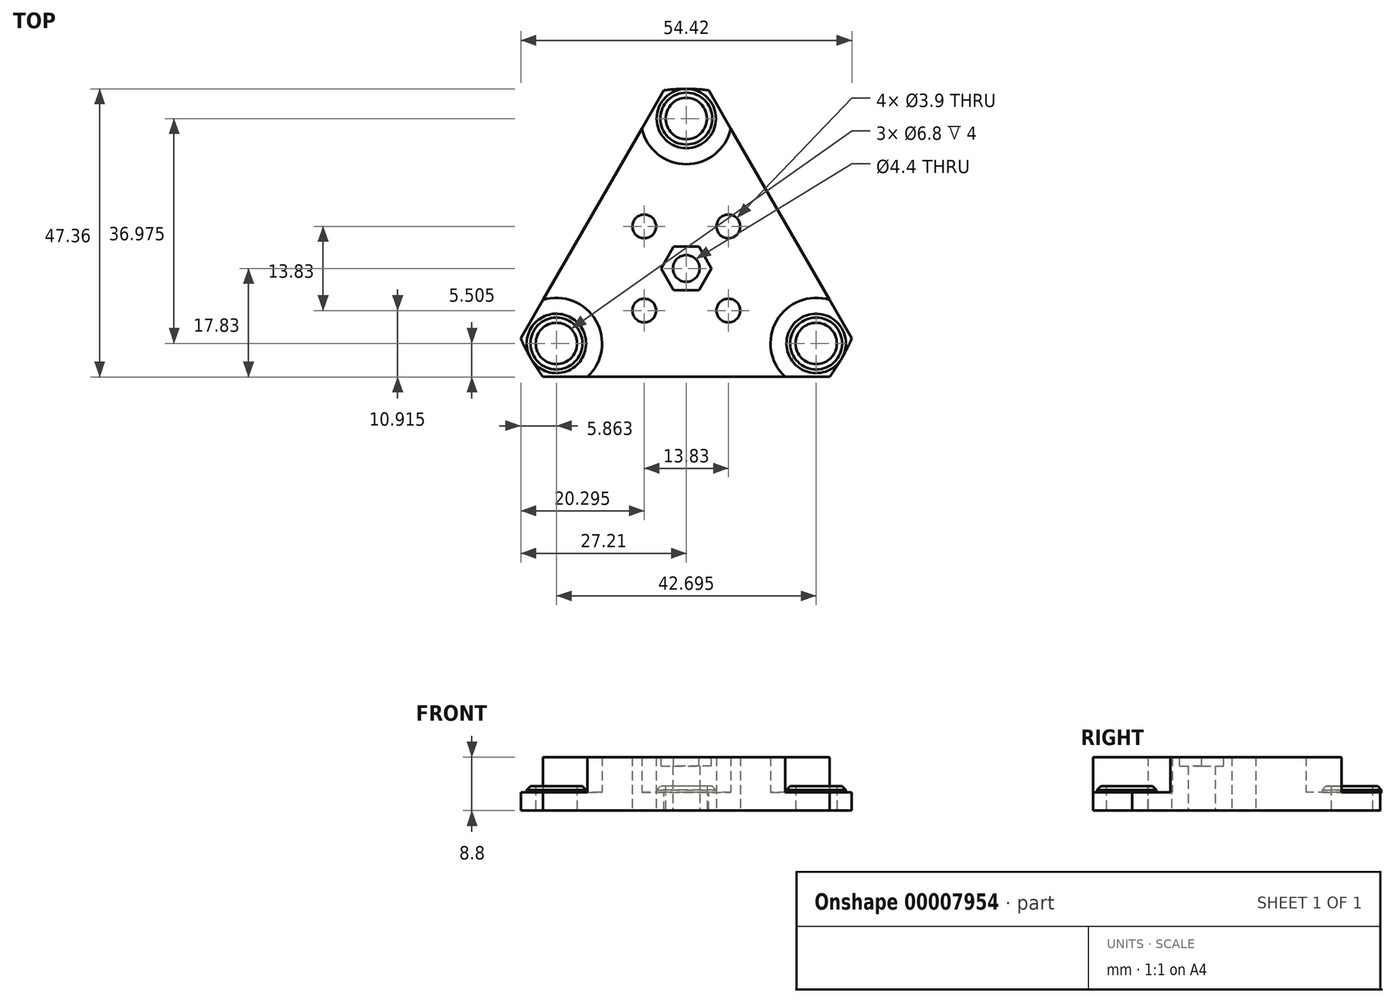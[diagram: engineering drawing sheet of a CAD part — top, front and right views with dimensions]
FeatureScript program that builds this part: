
annotation { "Feature Type Name" : "Feature", "Feature Type Description" : "" }
export const myFeature = defineFeature(function(context is Context, id is Id, definition is map)
    precondition{}
    {
        {
            var Q0;
            Q0=qCreatedBy(makeId("Top.planeOp"),FACE);
            var sketch = newSketch(context, id + "F0", { "sketchPlane" : qUnion([Q0])});
            skCircle(sketch, "E0", {"center": v(0, 0) * mm, "radius": 30 * mm, "construction": true});
            skCircle(sketch, "E1", {"center": v(0, 0) * mm, "radius": 31 * mm, "construction": true});
            skLineSegment(sketch, "E2", {"start": v(0, 30) * mm, "end": v(0, 31) * mm, "construction": true});
            skLineSegment(sketch, "E3", {"start": v(0, 30) * mm, "end": v(0, 0) * mm, "construction": true});
            skCircle(sketch, "E4", {"center": v(0, 24.65) * mm, "radius": 6.35 * mm, "construction": true});
            skCircle(sketch, "E5", {"center": v(0, 24.65) * mm, "radius": 3.4 * mm});
            skCircle(sketch, "E6.1.0", {"center": v(-21.35, -12.32) * mm, "radius": 3.4 * mm});
            skCircle(sketch, "E6.2.0", {"center": v(21.35, -12.33) * mm, "radius": 3.4 * mm});
            skLineSegment(sketch, "E7", {"start": v(-24.3, -14.02) * mm, "end": v(-26.85, -15.5) * mm, "construction": true});
            skPoint(sketch, "E8", {"position": v(-25.57, -14.76) * mm});
            skCircle(sketch, "E9", {"center": v(0, 0) * mm, "radius": 29.52 * mm});
            skSolve(sketch);
        }
        {
            var Q0;
            Q0=qSketchRegion(id+"F0",true);
            extrude(context, id + "F1", {"entities" : qUnion([Q0]), "depth" : 3 * mm});
        }
        {
            var Q0;
            Q0=makeQuery(id+"F1.opExtrude","CAP_FACE",FACE,{"disambiguationData":[OSD([sQuery(id+"F0.wireOp",EDGE,"E5"),sQuery(id+"F0.wireOp",EDGE,"E6.1.0"),sQuery(id+"F0.wireOp",EDGE,"E6.2.0"),sQuery(id+"F0.wireOp",EDGE,"E9")])],"isStart":false});
            var sketch = newSketch(context, id + "F2", { "sketchPlane" : qUnion([Q0])});
            skCircle(sketch, "E10", {"center": v(0, 24.65) * mm, "radius": 4.88 * mm});
            skCircle(sketch, "E11", {"center": v(21.35, -12.33) * mm, "radius": 4.88 * mm});
            skCircle(sketch, "E12", {"center": v(-21.35, -12.32) * mm, "radius": 4.87 * mm});
            skCircle(sketch, "E13.0", {"center": v(0, 24.65) * mm, "radius": 3.4 * mm});
            skCircle(sketch, "E13.1", {"center": v(-21.35, -12.32) * mm, "radius": 3.4 * mm});
            skCircle(sketch, "E13.2", {"center": v(21.35, -12.33) * mm, "radius": 3.4 * mm});
            skSolve(sketch);
        }
        {
            var Q0;
            Q0=qSketchRegion(id+"F2",true);
            extrude(context, id + "F3", {"entities" : qUnion([Q0]), "operationType" : NewBodyOperationType.ADD, "depth" : 1 * mm});
        }
        {
            var Q0;
            Q0=makeQuery(id+"F3.opExtrude","CAP_EDGE",EDGE,{"disambiguationData":[OSD([sQuery(id+"F2.wireOp",EDGE,"E12")])],"isStart":false});
            var Q1;
            Q1=makeQuery(id+"F3.opExtrude","CAP_EDGE",EDGE,{"disambiguationData":[OSD([sQuery(id+"F2.wireOp",EDGE,"E11")])],"isStart":false});
            var Q2;
            Q2=makeQuery(id+"F3.opExtrude","CAP_EDGE",EDGE,{"disambiguationData":[OSD([sQuery(id+"F2.wireOp",EDGE,"E10")])],"isStart":false});
            chamfer(context, id + "F4", {"entities" : qUnion([Q0, Q1, Q2]), "width" : 0.6 * mm, "tangentPropagation" : true});
        }
        {
            var Q0;
            Q0=makeQuery(id+"F1.opExtrude","CAP_FACE",FACE,{"disambiguationData":[OSD([sQuery(id+"F0.wireOp",EDGE,"E5"),sQuery(id+"F0.wireOp",EDGE,"E6.1.0"),sQuery(id+"F0.wireOp",EDGE,"E6.2.0"),sQuery(id+"F0.wireOp",EDGE,"E9")])],"isStart":false});
            var sketch = newSketch(context, id + "F5", { "sketchPlane" : qUnion([Q0])});
            skCircle(sketch, "E14", {"center": v(0, 24.65) * mm, "radius": 7.5 * mm, "construction": true});
            skCircle(sketch, "E15", {"center": v(-21.35, -12.32) * mm, "radius": 7.5 * mm, "construction": true});
            skCircle(sketch, "E16", {"center": v(21.35, -12.33) * mm, "radius": 7.5 * mm, "construction": true});
            skLineSegment(sketch, "E17", {"start": v(-6.5, 28.4) * mm, "end": v(-27.84, -8.58) * mm, "construction": true});
            skLineSegment(sketch, "E18", {"start": v(6.5, 28.4) * mm, "end": v(27.84, -8.58) * mm, "construction": true});
            skLineSegment(sketch, "E19", {"start": v(-21.35, -19.82) * mm, "end": v(21.35, -19.82) * mm, "construction": true});
            skLineSegment(sketch, "E20", {"start": v(-7.31, 22.98) * mm, "end": v(-23.56, -5.16) * mm});
            skLineSegment(sketch, "E21", {"start": v(7.31, 22.98) * mm, "end": v(23.56, -5.16) * mm});
            skLineSegment(sketch, "E22", {"start": v(16.25, -17.82) * mm, "end": v(-16.25, -17.82) * mm});
            skLineSegment(sketch, "E23", {"start": v(0, -17.82) * mm, "end": v(0, -19.82) * mm, "construction": true});
            skLineSegment(sketch, "E24", {"start": v(-15.44, 8.91) * mm, "end": v(-17.17, 9.91) * mm, "construction": true});
            skLineSegment(sketch, "E25", {"start": v(15.44, 8.91) * mm, "end": v(17.17, 9.91) * mm, "construction": true});
            skArc(sketch, "E26", {"start": v(-7.31, 22.98) * mm, "mid": v(0, 17.15) * mm, "end": v(7.31, 22.98) * mm});
            skArc(sketch, "E27", {"start": v(23.56, -5.16) * mm, "mid": v(14.85, -8.57) * mm, "end": v(16.25, -17.82) * mm});
            skArc(sketch, "E28", {"start": v(-16.25, -17.82) * mm, "mid": v(-14.85, -8.58) * mm, "end": v(-23.56, -5.16) * mm});
            skSolve(sketch);
        }
        {
            var Q0;
            Q0=qSketchRegion(id+"F5",true);
            extrude(context, id + "F6", {"entities" : qUnion([Q0]), "operationType" : NewBodyOperationType.ADD, "depth" : 5.8 * mm});
        }
        {
            var Q0;
            Q0=makeQuery(id+"F1.opExtrude","CAP_FACE",FACE,{"disambiguationData":[OSD([sQuery(id+"F0.wireOp",EDGE,"E5"),sQuery(id+"F0.wireOp",EDGE,"E6.1.0"),sQuery(id+"F0.wireOp",EDGE,"E6.2.0"),sQuery(id+"F0.wireOp",EDGE,"E9")])],"isStart":true});
            var sketch = newSketch(context, id + "F7", { "sketchPlane" : qUnion([Q0])});
            skLineSegment(sketch, "E29", {"start": v(0, 0) * mm, "end": v(0, -24.65) * mm, "construction": true});
            skCircle(sketch, "E30.cCircle", {"center": v(0, 0) * mm, "radius": 9.78 * mm, "construction": true});
            skLineSegment(sketch, "E30.0", {"start": v(6.91, -6.91) * mm, "end": v(-6.91, -6.91) * mm, "construction": true});
            skLineSegment(sketch, "E30.1", {"start": v(-6.91, -6.91) * mm, "end": v(-6.91, 6.91) * mm, "construction": true});
            skLineSegment(sketch, "E30.2", {"start": v(-6.91, 6.91) * mm, "end": v(6.91, 6.91) * mm, "construction": true});
            skLineSegment(sketch, "E30.3", {"start": v(6.91, 6.91) * mm, "end": v(6.91, -6.91) * mm, "construction": true});
            skCircle(sketch, "E31", {"center": v(6.91, 6.91) * mm, "radius": 1.95 * mm});
            skCircle(sketch, "E32.1.0", {"center": v(-6.91, 6.91) * mm, "radius": 1.95 * mm});
            skCircle(sketch, "E32.2.0", {"center": v(-6.91, -6.91) * mm, "radius": 1.95 * mm});
            skCircle(sketch, "E32.3.0", {"center": v(6.91, -6.91) * mm, "radius": 1.95 * mm});
            skSolve(sketch);
        }
        {
            var Q0;
            Q0=qSketchRegion(id+"F7",true);
            extrude(context, id + "F8", {"entities" : qUnion([Q0]), "operationType" : NewBodyOperationType.REMOVE, "endBound" : BoundingType.THROUGH_ALL, "oppositeDirection" : true, "depth" : 25 * mm});
        }
        {
            var Q0;
            Q0=makeQuery(id+"F6.opExtrude","CAP_FACE",FACE,{"disambiguationData":[OSD([sQuery(id+"F5.wireOp",EDGE,"E20"),sQuery(id+"F5.wireOp",EDGE,"E21"),sQuery(id+"F5.wireOp",EDGE,"E22"),sQuery(id+"F5.wireOp",EDGE,"b30b8c31-8519-46e4-bd01-4f495bb6e8cf"),sQuery(id+"F5.wireOp",EDGE,"E26"),sQuery(id+"F5.wireOp",EDGE,"E27")])],"isStart":false});
            var sketch = newSketch(context, id + "F9", { "sketchPlane" : qUnion([Q0])});
            skCircle(sketch, "E33.cCircle", {"center": v(0, 0) * mm, "radius": 3.6 * mm, "construction": true});
            skLineSegment(sketch, "E33.0", {"start": v(-2.08, 3.6) * mm, "end": v(2.08, 3.6) * mm});
            skLineSegment(sketch, "E33.1", {"start": v(2.08, 3.6) * mm, "end": v(4.16, 0) * mm});
            skLineSegment(sketch, "E33.2", {"start": v(4.16, 0) * mm, "end": v(2.08, -3.6) * mm});
            skLineSegment(sketch, "E33.3", {"start": v(2.08, -3.6) * mm, "end": v(-2.08, -3.6) * mm});
            skLineSegment(sketch, "E33.4", {"start": v(-2.08, -3.6) * mm, "end": v(-4.16, 0) * mm});
            skLineSegment(sketch, "E33.5", {"start": v(-4.16, 0) * mm, "end": v(-2.08, 3.6) * mm});
            skPoint(sketch, "E33.0.midPoint", {"position": v(0, 3.6) * mm});
            skSolve(sketch);
        }
        {
            var Q0;
            Q0=qSketchRegion(id+"F9",true);
            extrude(context, id + "F10", {"entities" : qUnion([Q0]), "operationType" : NewBodyOperationType.REMOVE, "oppositeDirection" : true, "depth" : 1.45 * mm});
        }
        {
            var Q0;
            Q0=makeQuery(id+"F1.opExtrude","CAP_FACE",FACE,{"disambiguationData":[OSD([sQuery(id+"F0.wireOp",EDGE,"E5"),sQuery(id+"F0.wireOp",EDGE,"E6.1.0"),sQuery(id+"F0.wireOp",EDGE,"E6.2.0"),sQuery(id+"F0.wireOp",EDGE,"E9")])],"isStart":true});
            var sketch = newSketch(context, id + "F11", { "sketchPlane" : qUnion([Q0])});
            skCircle(sketch, "E34", {"center": v(0, 0) * mm, "radius": 2.2 * mm});
            skSolve(sketch);
        }
        {
            var Q0;
            Q0 = qSketchRegion(id + "F11", true);
            extrude(context, id + "F12", {"entities" : qUnion([Q0]), "operationType" : NewBodyOperationType.REMOVE, "endBound" : BoundingType.THROUGH_ALL, "oppositeDirection" : true, "depth" : 25 * mm});
        }
        {
            var Q0;
            Q0=makeQuery(id+"F1.opExtrude","CAP_FACE",FACE,{"disambiguationData":[OSD([sQuery(id+"F0.wireOp",EDGE,"E5"),sQuery(id+"F0.wireOp",EDGE,"E6.1.0"),sQuery(id+"F0.wireOp",EDGE,"E6.2.0"),sQuery(id+"F0.wireOp",EDGE,"E9")])],"isStart":false});
            var sketch = newSketch(context, id + "F13", { "sketchPlane" : qUnion([Q0])});
            skLineSegment(sketch, "E35", {"start": v(27.2, -11.47) * mm, "end": v(3.67, 29.3) * mm});
            skLineSegment(sketch, "E36.1.0", {"start": v(-3.67, 29.3) * mm, "end": v(-27.2, -11.47) * mm});
            skLineSegment(sketch, "E36.2.0", {"start": v(-23.54, -17.82) * mm, "end": v(23.54, -17.82) * mm});
            skPoint(sketch, "E36.center", {"position": v(0, 0) * mm});
            skArc(sketch, "E37.0", {"start": v(-3.67, 29.3) * mm, "mid": v(-25.57, 14.76) * mm, "end": v(-27.2, -11.47) * mm});
            skArc(sketch, "E38.0", {"start": v(27.2, -11.47) * mm, "mid": v(25.57, 14.76) * mm, "end": v(3.67, 29.3) * mm});
            skArc(sketch, "E39.0", {"start": v(-23.54, -17.82) * mm, "mid": v(0, -29.53) * mm, "end": v(23.54, -17.82) * mm});
            skPoint(sketch, "E40.orphan", {"position": v(-25.57, -14.76) * mm});
            skPoint(sketch, "E41.orphan", {"position": v(0, 29.52) * mm});
            skPoint(sketch, "E42.orphan", {"position": v(25.57, -14.76) * mm});
            skSolve(sketch);
        }
        {
            var Q0;
            Q0 = qSketchRegion(id + "F13", true);
            extrude(context, id + "F14", {"entities" : qUnion([Q0]), "operationType" : NewBodyOperationType.REMOVE, "endBound" : BoundingType.THROUGH_ALL, "oppositeDirection" : true, "depth" : 25 * mm});
        }
    });
